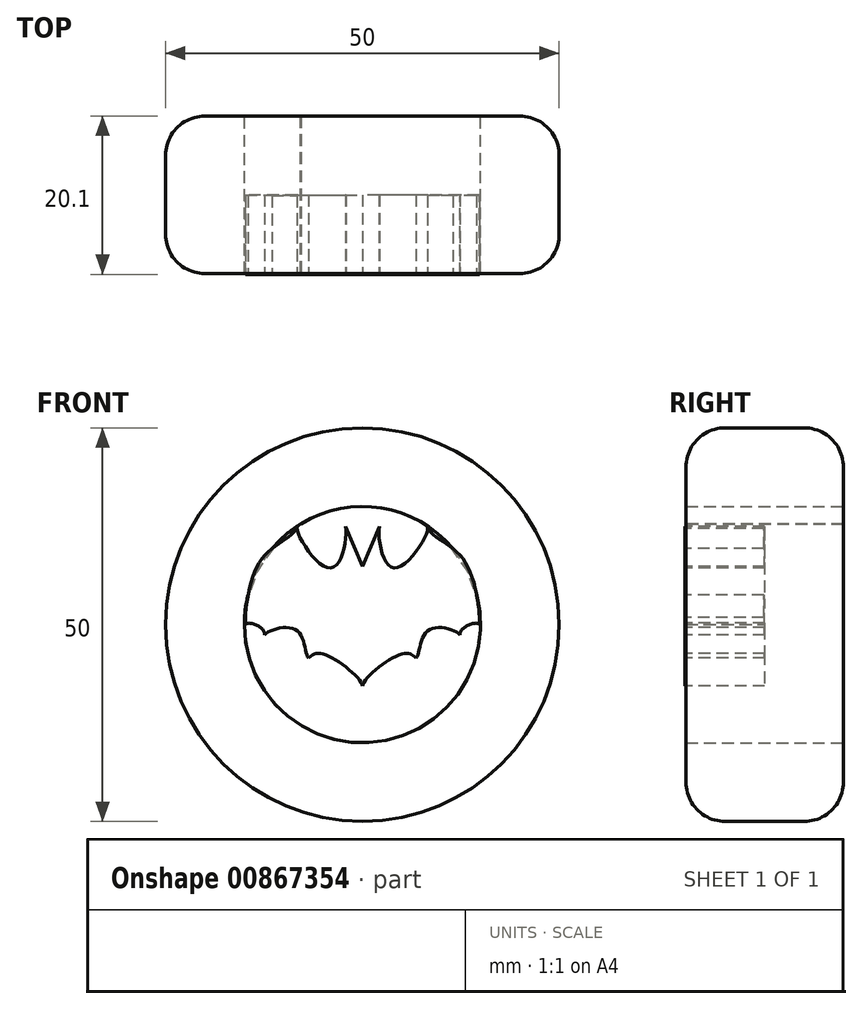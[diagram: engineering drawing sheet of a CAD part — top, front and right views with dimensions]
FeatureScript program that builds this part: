
annotation { "Feature Type Name" : "Feature", "Feature Type Description" : "" }
export const myFeature = defineFeature(function(context is Context, id is Id, definition is map)
    precondition{}
    {
        {
            var Q0;
            Q0=qCreatedBy(makeId("Front.planeOp"),FACE);
            var sketch = newSketch(context, id + "F0", { "sketchPlane" : qUnion([Q0])});
            skCircle(sketch, "E0", {"center": v(0, 0) * mm, "radius": 15 * mm});
            skCircle(sketch, "E1", {"center": v(0, 0) * mm, "radius": 25 * mm});
            skSolve(sketch);
        }
        {
            var Q0;
            Q0=makeQuery(id+"F0.imprint","IMPRINT",FACE,{"disambiguationData":[TD([[makeQuery(id+"F0.imprint","IMPRINT",EDGE,{"derivedFrom":sQuery(id+"F0.wireOp",EDGE,"E0")}),-1.0]])]});
            extrude(context, id + "F1", {"entities" : qUnion([Q0]), "endBound" : BoundingType.SYMMETRIC, "depth" : 20 * mm, "offsetDistance" : 25 * mm});
        }
        {
            var Q0;
            Q0=qCreatedBy(makeId("Front.planeOp"),FACE);
            var sketch = newSketch(context, id + "F2", { "sketchPlane" : qUnion([Q0])});
            skLineSegment(sketch, "E2", {"start": v(0, -7.88) * mm, "end": v(-14.86, 0) * mm});
            skLineSegment(sketch, "E3", {"start": v(-14.86, 0) * mm, "end": v(-14.86, 12.49) * mm});
            skLineSegment(sketch, "E4", {"start": v(-14.86, 12.49) * mm, "end": v(0, 12.49) * mm});
            skLineSegment(sketch, "E5", {"start": v(0, 12.49) * mm, "end": v(0, -7.88) * mm});
            skSolve(sketch);
        }
        {
            var Q0;
            Q0=makeQuery(id+"F2.imprint","IMPRINT",FACE,{"disambiguationData":[TD([[makeQuery(id+"F2.imprint","IMPRINT",EDGE,{"derivedFrom":sQuery(id+"F2.wireOp",EDGE,"E2")}),-1.0]])]});
            extrude(context, id + "F3", {"entities" : qUnion([Q0]), "operationType" : NewBodyOperationType.ADD, "depth" : 10.1 * mm, "offsetDistance" : 25 * mm});
        }
        {
            var Q0;
            Q0=makeQuery(id+"F3.opExtrude","CAP_FACE",FACE,{"disambiguationData":[OSD([sQuery(id+"F2.wireOp",EDGE,"E2"),sQuery(id+"F2.wireOp",EDGE,"E3"),sQuery(id+"F2.wireOp",EDGE,"E4"),sQuery(id+"F2.wireOp",EDGE,"E5")])],"isStart":false});
            var sketch = newSketch(context, id + "F4", { "sketchPlane" : qUnion([Q0])});
            skFitSpline(sketch, "E6", {"points": [v(-14.86, 0) * mm, v(-13.76, 9.42) * mm, v(-8.09, 12.49) * mm, v(-16.09, 14.34) * mm, v(-18, 7.44) * mm, v(-14.86, 0) * mm]});
            skSolve(sketch);
        }
        {
            var Q0;
            {var subQ1=makeQuery(id+"F3.opExtrude","CAP_EDGE",EDGE,{"disambiguationData":[OSD([sQuery(id+"F2.wireOp",EDGE,"E3")])],"isStart":false});var subQ3=sQuery(id+"F4.wireOp",EDGE,"E6");var subQ7=makeQuery(id+"F4.imprint","INTERSECT",VERTEX,{"disambiguationData":[OD(0.0)],"derivedFrom":[subQ1,subQ3]});Q0=makeQuery(id+"F4.imprint","IMPRINT",FACE,{"disambiguationData":[TD([[makeQuery(id+"F4.imprint","IMPRINT",EDGE,{"disambiguationData":[TD([[subQ7,-1.0]])],"derivedFrom":subQ3}),1.0]])]});}
            var Q1;
            {var subQ0=sQuery(id+"F4.wireOp",EDGE,"E6");var subQ1=makeQuery(id+"F3.opExtrude","CAP_EDGE",EDGE,{"disambiguationData":[OSD([sQuery(id+"F2.wireOp",EDGE,"E4")])],"isStart":false});var subQ2=makeQuery(id+"F4.imprint","INTERSECT",VERTEX,{"derivedFrom":[subQ1,subQ0]});Q1=makeQuery(id+"F4.imprint","IMPRINT",FACE,{"disambiguationData":[TD([[makeQuery(id+"F4.imprint","IMPRINT",EDGE,{"disambiguationData":[TD([[subQ2,1.0]])],"derivedFrom":subQ0}),1.0]])]});}
            extrude(context, id + "F5", {"entities" : qUnion([Q0, Q1]), "operationType" : NewBodyOperationType.REMOVE, "oppositeDirection" : true, "depth" : 10 * mm, "offsetDistance" : 25 * mm});
        }
        {
            var Q0;
            Q0=makeQuery(id+"F3.opExtrude","CAP_FACE",FACE,{"disambiguationData":[OSD([sQuery(id+"F2.wireOp",EDGE,"E2"),sQuery(id+"F2.wireOp",EDGE,"E3"),sQuery(id+"F2.wireOp",EDGE,"E4"),sQuery(id+"F2.wireOp",EDGE,"E5")])],"isStart":false});
            var sketch = newSketch(context, id + "F6", { "sketchPlane" : qUnion([Q0])});
            skFitSpline(sketch, "E7", {"points": [v(-14.86, 0) * mm, v(-12.93, 8.14) * mm, v(-8.09, 12.49) * mm, v(-8.09, 16.07) * mm, v(-19.83, 2.73) * mm, v(-16.15, -1.18) * mm, v(-14.86, -0.77) * mm, v(-14.86, 0) * mm]});
            skSolve(sketch);
        }
        {
            var Q0;
            {var subQ0=sQuery(id+"F6.wireOp",EDGE,"E7");var subQ1=makeQuery(id+"F3.opExtrude","CAP_EDGE",EDGE,{"disambiguationData":[OSD([sQuery(id+"F2.wireOp",EDGE,"E3")])],"isStart":false});var subQ2=makeQuery(id+"F6.imprint","INTERSECT",VERTEX,{"derivedFrom":[subQ1,subQ0]});Q0=makeQuery(id+"F6.imprint","IMPRINT",FACE,{"disambiguationData":[TD([[makeQuery(id+"F6.imprint","IMPRINT",EDGE,{"disambiguationData":[TD([[subQ2,-1.0]])],"derivedFrom":subQ0}),1.0]])]});}
            extrude(context, id + "F7", {"entities" : qUnion([Q0]), "operationType" : NewBodyOperationType.REMOVE, "oppositeDirection" : true, "depth" : 10 * mm, "offsetDistance" : 25 * mm});
        }
        {
            var Q0;
            Q0=makeQuery(id+"F3.opExtrude","CAP_FACE",FACE,{"disambiguationData":[OSD([sQuery(id+"F2.wireOp",EDGE,"E2"),sQuery(id+"F2.wireOp",EDGE,"E3"),sQuery(id+"F2.wireOp",EDGE,"E4"),sQuery(id+"F2.wireOp",EDGE,"E5")])],"isStart":false});
            var sketch = newSketch(context, id + "F8", { "sketchPlane" : qUnion([Q0])});
            skFitSpline(sketch, "E8", {"points": [v(-14.86, 0) * mm, v(-13.58, 0) * mm, v(-12.42, -1.3) * mm, v(-13.4, -2.14) * mm, v(-13.92, -1.56) * mm, v(-14.45, -1.08) * mm, v(-14.86, 0) * mm]});
            skSolve(sketch);
        }
        {
            var Q0;
            {var subQ0=sQuery(id+"F8.wireOp",EDGE,"E8");var subQ1=makeQuery(id+"F3.opExtrude","CAP_EDGE",EDGE,{"disambiguationData":[OSD([sQuery(id+"F2.wireOp",EDGE,"E2")])],"isStart":false});var subQ3=makeQuery(id+"F8.imprint","INTERSECT",VERTEX,{"derivedFrom":[subQ1,subQ0]});Q0=makeQuery(id+"F8.imprint","IMPRINT",FACE,{"disambiguationData":[TD([[makeQuery(id+"F8.imprint","IMPRINT",EDGE,{"disambiguationData":[TD([[subQ3,1.0]])],"derivedFrom":subQ0}),-1.0]])]});}
            var Q1;
            Q1=sQuery(id+"F8.wireOp",EDGE,"E8");
            extrude(context, id + "F9", {"entities" : qUnion([Q0]), "operationType" : NewBodyOperationType.REMOVE, "surfaceEntities" : qUnion([Q1]), "oppositeDirection" : true, "depth" : 25 * mm, "offsetDistance" : 25 * mm});
        }
        {
            var Q0;
            Q0=makeQuery(id+"F3.opExtrude","CAP_FACE",FACE,{"disambiguationData":[OSD([sQuery(id+"F2.wireOp",EDGE,"E2"),sQuery(id+"F2.wireOp",EDGE,"E3"),sQuery(id+"F2.wireOp",EDGE,"E4"),sQuery(id+"F2.wireOp",EDGE,"E5")])],"isStart":false});
            var sketch = newSketch(context, id + "F10", { "sketchPlane" : qUnion([Q0])});
            skFitSpline(sketch, "E9", {"points": [v(-12.42, -1.3) * mm, v(-8.34, -0.74) * mm, v(-6.82, -4.26) * mm, v(-6.2, -4.59) * mm, v(-7.52, -6.44) * mm, v(-10.9, -5) * mm, v(-11.87, -3.64) * mm, v(-12.42, -2.33) * mm, v(-12.42, -1.3) * mm]});
            skSolve(sketch);
        }
        {
            var Q0;
            {var subQ0=sQuery(id+"F10.wireOp",EDGE,"E9");var subQ1=makeQuery(id+"F3.opExtrude","CAP_EDGE",EDGE,{"disambiguationData":[OSD([sQuery(id+"F2.wireOp",EDGE,"E2")])],"isStart":false});var subQ3=makeQuery(id+"F10.imprint","INTERSECT",VERTEX,{"disambiguationData":[OD(1.0)],"derivedFrom":[subQ1,subQ0]});Q0=makeQuery(id+"F10.imprint","IMPRINT",FACE,{"disambiguationData":[TD([[makeQuery(id+"F10.imprint","IMPRINT",EDGE,{"disambiguationData":[TD([[subQ3,1.0]])],"derivedFrom":subQ0}),-1.0]])]});}
            extrude(context, id + "F11", {"entities" : qUnion([Q0]), "operationType" : NewBodyOperationType.REMOVE, "oppositeDirection" : true, "depth" : 25 * mm, "offsetDistance" : 25 * mm});
        }
        {
            var Q0;
            Q0=makeQuery(id+"F3.opExtrude","CAP_FACE",FACE,{"disambiguationData":[OSD([sQuery(id+"F2.wireOp",EDGE,"E2"),sQuery(id+"F2.wireOp",EDGE,"E3"),sQuery(id+"F2.wireOp",EDGE,"E4"),sQuery(id+"F2.wireOp",EDGE,"E5")])],"isStart":false});
            var sketch = newSketch(context, id + "F12", { "sketchPlane" : qUnion([Q0])});
            skPoint(sketch, "E10.6.internal.snap0", {"position": v(-3.41, -6.07) * mm});
            skFitSpline(sketch, "E10", {"points": [v(-6.82, -4.26) * mm, v(-4.86, -3.78) * mm, v(0, -7.88) * mm, v(-1.24, -8.33) * mm, v(-2.64, -7.88) * mm, v(-6.07, -7.88) * mm, v(-7.42, -6.07) * mm, v(-6.82, -4.26) * mm]});
            skSolve(sketch);
        }
        {
            var Q0;
            {var subQ1=makeQuery(id+"F3.opExtrude","CAP_EDGE",EDGE,{"disambiguationData":[OSD([sQuery(id+"F2.wireOp",EDGE,"E2")])],"isStart":false});Q0=makeQuery(id+"F12.imprint","IMPRINT",FACE,{"disambiguationData":[TD([[makeQuery(id+"F12.imprint","IMPRINT",EDGE,{"derivedFrom":subQ1}),-1.0]])]});}
            extrude(context, id + "F13", {"entities" : qUnion([Q0]), "operationType" : NewBodyOperationType.REMOVE, "oppositeDirection" : true, "depth" : 25 * mm, "offsetDistance" : 25 * mm});
        }
        {
            var Q0;
            Q0=makeQuery(id+"F3.opExtrude","CAP_FACE",FACE,{"disambiguationData":[OSD([sQuery(id+"F2.wireOp",EDGE,"E2"),sQuery(id+"F2.wireOp",EDGE,"E3"),sQuery(id+"F2.wireOp",EDGE,"E4"),sQuery(id+"F2.wireOp",EDGE,"E5")])],"isStart":false});
            var sketch = newSketch(context, id + "F14", { "sketchPlane" : qUnion([Q0])});
            skFitSpline(sketch, "E11", {"points": [v(-8.28, 12.22) * mm, v(-4.06, 7.19) * mm, v(-2.16, 12.49) * mm, v(-3.02, 13.4) * mm, v(-4.23, 13.4) * mm, v(-5.78, 13.28) * mm, v(-7.34, 12.49) * mm, v(-8.28, 12.22) * mm]});
            skSolve(sketch);
        }
        {
            var Q0;
            {var subQ0=sQuery(id+"F14.wireOp",EDGE,"E11");var subQ3=makeQuery(id+"F3.opExtrude","CAP_EDGE",EDGE,{"disambiguationData":[OSD([sQuery(id+"F2.wireOp",EDGE,"E4")])],"isStart":false});var subQ5=makeQuery(id+"F14.imprint","INTERSECT",VERTEX,{"disambiguationData":[OD(1.0)],"derivedFrom":[subQ3,subQ0]});Q0=makeQuery(id+"F14.imprint","IMPRINT",FACE,{"disambiguationData":[TD([[makeQuery(id+"F14.imprint","IMPRINT",EDGE,{"disambiguationData":[TD([[subQ5,-1.0]])],"derivedFrom":subQ0}),1.0]])]});}
            extrude(context, id + "F15", {"entities" : qUnion([Q0]), "operationType" : NewBodyOperationType.REMOVE, "oppositeDirection" : true, "depth" : 25 * mm, "offsetDistance" : 25 * mm});
        }
        {
            var Q0;
            {var subQ1=sQuery(id+"F2.wireOp",EDGE,"E4");var subQ2=sQuery(id+"F2.wireOp",EDGE,"E5");var subQ3=sQuery(id+"F2.wireOp",EDGE,"E3");Q0=makeQuery(id+"F15.boolean.opBoolean","SPLIT",FACE,{"disambiguationData":[TD([makeQuery(id+"F3.opExtrude","SWEPT_FACE",FACE,{"disambiguationData":[OSD([subQ3])]})])],"derivedFrom":makeQuery(id+"F3.opExtrude","CAP_FACE",FACE,{"disambiguationData":[OSD([sQuery(id+"F2.wireOp",EDGE,"E2"),subQ3,subQ1,subQ2])],"isStart":false})});}
            var sketch = newSketch(context, id + "F16", { "sketchPlane" : qUnion([Q0])});
            skLineSegment(sketch, "E12", {"start": v(-2.16, 12.49) * mm, "end": v(0, 7.42) * mm});
            skLineSegment(sketch, "E13", {"start": v(0, 7.42) * mm, "end": v(0, 12.49) * mm});
            skLineSegment(sketch, "E14", {"start": v(0, 12.49) * mm, "end": v(-2.16, 12.49) * mm});
            skSolve(sketch);
        }
        {
            var Q0;
            Q0=makeQuery(id+"F16.imprint","IMPRINT",FACE,{"disambiguationData":[TD([[makeQuery(id+"F16.imprint","IMPRINT",EDGE,{"derivedFrom":sQuery(id+"F16.wireOp",EDGE,"E12")}),1.0]])]});
            extrude(context, id + "F17", {"entities" : qUnion([Q0]), "operationType" : NewBodyOperationType.REMOVE, "oppositeDirection" : true, "depth" : 25 * mm, "offsetDistance" : 25 * mm});
        }
        {
            var Q0;
            {var subQ1=sQuery(id+"F2.wireOp",EDGE,"E4");var subQ2=sQuery(id+"F2.wireOp",EDGE,"E5");var subQ3=sQuery(id+"F2.wireOp",EDGE,"E3");Q0=makeQuery(id+"F15.boolean.opBoolean","SPLIT",FACE,{"disambiguationData":[TD([makeQuery(id+"F3.opExtrude","SWEPT_FACE",FACE,{"disambiguationData":[OSD([subQ3])]})])],"derivedFrom":makeQuery(id+"F3.opExtrude","CAP_FACE",FACE,{"disambiguationData":[OSD([sQuery(id+"F2.wireOp",EDGE,"E2"),subQ3,subQ1,subQ2])],"isStart":false})});}
            var sketch = newSketch(context, id + "F18", { "sketchPlane" : qUnion([Q0])});
            skFitSpline(sketch, "E15", {"points": [v(-8.28, 12.22) * mm, v(-6.65, 12.22) * mm, v(-7.05, 13) * mm, v(-8.28, 12.22) * mm]});
            skSolve(sketch);
        }
        {
            var Q0;
            Q0=makeQuery(id+"F18.imprint","IMPRINT",FACE,{"disambiguationData":[TD([[makeQuery(id+"F18.imprint","IMPRINT",EDGE,{"derivedFrom":sQuery(id+"F18.wireOp",EDGE,"E15")}),1.0]])]});
            extrude(context, id + "F19", {"entities" : qUnion([Q0]), "operationType" : NewBodyOperationType.REMOVE, "oppositeDirection" : true, "depth" : 25 * mm, "offsetDistance" : 25 * mm});
        }
        {
            var Q0;
            Q0=makeQuery(id+"F1.opExtrude","SWEPT_BODY",BODY,{"disambiguationData":[OSD([sQuery(id+"F0.wireOp",EDGE,"E0"),sQuery(id+"F0.wireOp",EDGE,"E1")])]});
            var Q1;
            Q1=qCreatedBy(makeId("Right.planeOp"),FACE);
            mirror(context, id + "F20", {"operationType" : NewBodyOperationType.ADD, "entities" : qUnion([Q0]), "mirrorPlane" : qUnion([Q1])});
        }
        {
            var Q0;
            Q0=makeQuery(id+"F1.opExtrude","CAP_EDGE",EDGE,{"disambiguationData":[OSD([sQuery(id+"F0.wireOp",EDGE,"E1")])],"isStart":false});
            var Q1;
            Q1=makeQuery(id+"F1.opExtrude","CAP_EDGE",EDGE,{"disambiguationData":[OSD([sQuery(id+"F0.wireOp",EDGE,"E1")])],"isStart":true});
            fillet(context, id + "F21", {"entities" : qUnion([Q0, Q1]), "radius" : 5 * mm, "tangentPropagation" : true, "allowEdgeOverflow" : false});
        }
    });
